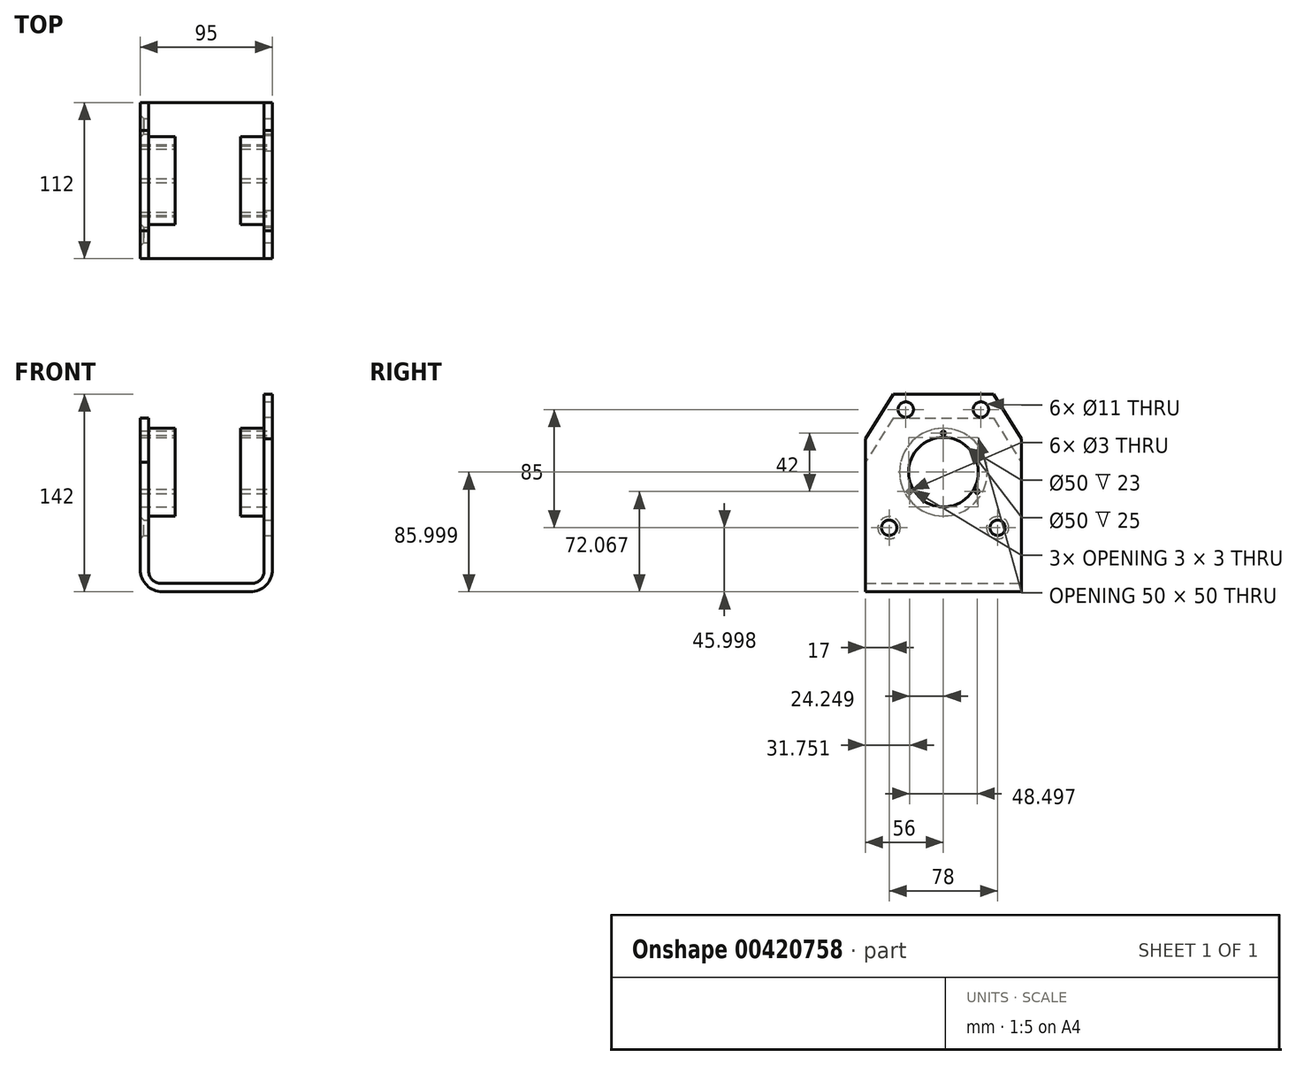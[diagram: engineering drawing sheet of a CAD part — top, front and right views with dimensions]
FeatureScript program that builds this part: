
annotation { "Feature Type Name" : "Feature", "Feature Type Description" : "" }
export const myFeature = defineFeature(function(context is Context, id is Id, definition is map)
    precondition{}
    {
        {
            var Q0;
            Q0=qCreatedBy(makeId("Front.planeOp"),FACE);
            var sketch = newSketch(context, id + "F0", { "sketchPlane" : qUnion([Q0])});
            skLineSegment(sketch, "E0.top", {"start": v(-43.8, -38.82) * mm, "end": v(19.2, -38.82) * mm});
            skLineSegment(sketch, "E0.right", {"start": v(35.2, 103.18) * mm, "end": v(35.2, -22.82) * mm});
            skLineSegment(sketch, "E1.top", {"start": v(-44.8, -32.82) * mm, "end": v(20.2, -32.82) * mm});
            skLineSegment(sketch, "E1.right", {"start": v(29.2, 103.18) * mm, "end": v(29.2, -23.82) * mm});
            skLineSegment(sketch, "E2", {"start": v(29.2, 103.18) * mm, "end": v(35.2, 103.18) * mm});
            skLineSegment(sketch, "E3.right", {"start": v(29.2, 103.18) * mm, "end": v(29.2, 87.18) * mm});
            skLineSegment(sketch, "E4", {"start": v(-53.8, -23.82) * mm, "end": v(-53.8, 86.18) * mm});
            skLineSegment(sketch, "E5", {"start": v(-53.8, 86.18) * mm, "end": v(-59.8, 86.18) * mm});
            skLineSegment(sketch, "E6", {"start": v(-59.8, 86.18) * mm, "end": v(-59.8, -22.82) * mm});
            skPoint(sketch, "E7.visualSharp", {"position": v(-53.8, -32.82) * mm});
            skArc(sketch, "E7.filletArc", {"start": v(-53.8, -23.82) * mm, "mid": v(-51.16, -30.19) * mm, "end": v(-44.8, -32.82) * mm});
            skPoint(sketch, "E8.visualSharp", {"position": v(-59.8, -38.82) * mm});
            skArc(sketch, "E8.filletArc", {"start": v(-59.8, -22.82) * mm, "mid": v(-55.1, -34.14) * mm, "end": v(-43.8, -38.82) * mm});
            skPoint(sketch, "E9.visualSharp", {"position": v(29.2, -32.82) * mm});
            skArc(sketch, "E9.filletArc", {"start": v(20.2, -32.82) * mm, "mid": v(26.57, -30.19) * mm, "end": v(29.2, -23.82) * mm});
            skPoint(sketch, "E10.visualSharp", {"position": v(35.2, -38.82) * mm});
            skArc(sketch, "E10.filletArc", {"start": v(19.2, -38.82) * mm, "mid": v(30.52, -34.14) * mm, "end": v(35.2, -22.82) * mm});
            skSolve(sketch);
        }
        {
            var Q0;
            Q0=makeQuery(id+"F0.imprint","IMPRINT",FACE,{"disambiguationData":[TD([[makeQuery(id+"F0.imprint","IMPRINT",EDGE,{"derivedFrom":sQuery(id+"F0.wireOp",EDGE,"E0.top")}),1.0]])]});
            extrude(context, id + "F1", {"entities" : qUnion([Q0]), "depth" : 112 * mm});
        }
        {
            var Q0;
            Q0=makeQuery(id+"F1.opExtrude","SWEPT_FACE",FACE,{"disambiguationData":[OSD([sQuery(id+"F0.wireOp",EDGE,"E0.right")])]});
            var sketch = newSketch(context, id + "F2", { "sketchPlane" : qUnion([Q0])});
            skCircle(sketch, "E11", {"center": v(-56, 47.18) * mm, "radius": 25 * mm});
            skCircle(sketch, "E12", {"center": v(-56, 47.18) * mm, "radius": 31.5 * mm});
            skSolve(sketch);
        }
        {
            var Q0;
            Q0=makeQuery(id+"F2.imprint","IMPRINT",FACE,{"disambiguationData":[TD([[makeQuery(id+"F2.imprint","IMPRINT",EDGE,{"derivedFrom":sQuery(id+"F2.wireOp",EDGE,"E11")}),1.0]])]});
            extrude(context, id + "F3", {"entities" : qUnion([Q0]), "operationType" : NewBodyOperationType.REMOVE, "oppositeDirection" : true, "depth" : 185 * mm});
        }
        {
            var Q0;
            Q0=makeQuery(id+"F1.opExtrude","CAP_FACE",FACE,{"disambiguationData":[OSD([sQuery(id+"F0.wireOp",EDGE,"E0.top"),sQuery(id+"F0.wireOp",EDGE,"E0.right"),sQuery(id+"F0.wireOp",EDGE,"E1.top"),sQuery(id+"F0.wireOp",EDGE,"E1.right"),sQuery(id+"F0.wireOp",EDGE,"E2"),sQuery(id+"F0.wireOp",EDGE,"E3.right"),sQuery(id+"F0.wireOp",EDGE,"E4"),sQuery(id+"F0.wireOp",EDGE,"E5"),sQuery(id+"F0.wireOp",EDGE,"E6"),sQuery(id+"F0.wireOp",EDGE,"E7.filletArc"),sQuery(id+"F0.wireOp",EDGE,"E8.filletArc"),sQuery(id+"F0.wireOp",EDGE,"E9.filletArc"),sQuery(id+"F0.wireOp",EDGE,"E10.filletArc")])],"isStart":false});
            cPlane(context, id + "F4", {"entities" : qUnion([Q0]), "cplaneType" : CPlaneType.OFFSET, "offset" : 25 * mm, "width" : 150 * mm, "height" : 150 * mm});
        }
        {
            var Q0;
            Q0=makeQuery(id+"F2.imprint","IMPRINT",FACE,{"disambiguationData":[TD([[makeQuery(id+"F2.imprint","IMPRINT",EDGE,{"derivedFrom":sQuery(id+"F2.wireOp",EDGE,"E11")}),-1.0]])]});
            extrude(context, id + "F5", {"entities" : qUnion([Q0]), "operationType" : NewBodyOperationType.REMOVE, "oppositeDirection" : true, "depth" : 184 * mm});
        }
        {
            var Q0;
            Q0=makeQuery(id+"F2.imprint","IMPRINT",FACE,{"disambiguationData":[TD([[makeQuery(id+"F2.imprint","IMPRINT",EDGE,{"derivedFrom":sQuery(id+"F2.wireOp",EDGE,"E11")}),-1.0]])]});
            extrude(context, id + "F6", {"entities" : qUnion([Q0]), "operationType" : NewBodyOperationType.ADD, "oppositeDirection" : true, "depth" : 95 * mm});
        }
        {
            var Q0;
            Q0=qCreatedBy(id+"F4.planeOp",FACE);
            var sketch = newSketch(context, id + "F7", { "sketchPlane" : qUnion([Q0])});
            skLineSegment(sketch, "E13.bottom", {"start": v(-34.8, 79.18) * mm, "end": v(12.2, 79.18) * mm});
            skLineSegment(sketch, "E13.top", {"start": v(-34.8, -20.82) * mm, "end": v(12.2, -20.82) * mm});
            skLineSegment(sketch, "E13.left", {"start": v(-34.8, 79.18) * mm, "end": v(-34.8, -20.82) * mm});
            skLineSegment(sketch, "E13.right", {"start": v(12.2, 79.18) * mm, "end": v(12.2, -20.82) * mm});
            skSolve(sketch);
        }
        {
            var Q0;
            Q0=makeQuery(id+"F7.imprint","IMPRINT",FACE,{"disambiguationData":[TD([[makeQuery(id+"F7.imprint","IMPRINT",EDGE,{"derivedFrom":sQuery(id+"F7.wireOp",EDGE,"E13.bottom")}),-1.0]])]});
            extrude(context, id + "F8", {"entities" : qUnion([Q0]), "operationType" : NewBodyOperationType.REMOVE, "oppositeDirection" : true, "depth" : 159 * mm});
        }
        {
            var Q0;
            Q0=makeQuery(id+"F2.imprint","IMPRINT",FACE,{"disambiguationData":[TD([[makeQuery(id+"F2.imprint","IMPRINT",EDGE,{"derivedFrom":sQuery(id+"F2.wireOp",EDGE,"E12")}),-1.0]])]});
            var sketch = newSketch(context, id + "F9", { "sketchPlane" : qUnion([Q0])});
            skCircle(sketch, "E14", {"center": v(-83, 92.18) * mm, "radius": 5.5 * mm});
            skCircle(sketch, "E15", {"center": v(-29, 92.18) * mm, "radius": 5.5 * mm});
            skCircle(sketch, "E16", {"center": v(-95, 7.18) * mm, "radius": 5.5 * mm});
            skCircle(sketch, "E17", {"center": v(-17, 7.18) * mm, "radius": 5.5 * mm});
            skPoint(sketch, "E18", {"position": v(-56, 47.25) * mm});
            skPoint(sketch, "E19", {"position": v(-80.25, 33.25) * mm});
            skPoint(sketch, "E20", {"position": v(-31.75, 33.25) * mm});
            skPoint(sketch, "E21", {"position": v(-56, 75.25) * mm});
            skCircle(sketch, "E22", {"center": v(-80.25, 33.25) * mm, "radius": 1.5 * mm});
            skCircle(sketch, "E23", {"center": v(-56, 75.25) * mm, "radius": 1.5 * mm});
            skCircle(sketch, "E24", {"center": v(-31.75, 33.25) * mm, "radius": 1.5 * mm});
            skLineSegment(sketch, "E25", {"start": v(-56, 75.25) * mm, "end": v(-56, 47.25) * mm});
            skSolve(sketch);
        }
        {
            var Q0;
            Q0=makeQuery(id+"F9.imprint","IMPRINT",FACE,{"disambiguationData":[TD([[makeQuery(id+"F9.imprint","IMPRINT",EDGE,{"derivedFrom":sQuery(id+"F9.wireOp",EDGE,"E14")}),1.0]])]});
            var Q1;
            Q1=makeQuery(id+"F9.imprint","IMPRINT",FACE,{"disambiguationData":[TD([[makeQuery(id+"F9.imprint","IMPRINT",EDGE,{"derivedFrom":sQuery(id+"F9.wireOp",EDGE,"E15")}),1.0]])]});
            var Q2;
            Q2=makeQuery(id+"F9.imprint","IMPRINT",FACE,{"disambiguationData":[TD([[makeQuery(id+"F9.imprint","IMPRINT",EDGE,{"derivedFrom":sQuery(id+"F9.wireOp",EDGE,"E16")}),1.0]])]});
            var Q3;
            Q3=makeQuery(id+"F9.imprint","IMPRINT",FACE,{"disambiguationData":[TD([[makeQuery(id+"F9.imprint","IMPRINT",EDGE,{"derivedFrom":sQuery(id+"F9.wireOp",EDGE,"E17")}),1.0]])]});
            extrude(context, id + "F10", {"entities" : qUnion([Q0, Q1, Q2, Q3]), "operationType" : NewBodyOperationType.REMOVE, "oppositeDirection" : true, "depth" : 157.2 * mm});
        }
        {
            var Q0;
            Q0=makeQuery(id+"F9.imprint","IMPRINT",FACE,{"disambiguationData":[TD([[makeQuery(id+"F9.imprint","IMPRINT",EDGE,{"derivedFrom":sQuery(id+"F9.wireOp",EDGE,"E24")}),1.0]])]});
            var Q1;
            Q1=makeQuery(id+"F9.imprint","IMPRINT",FACE,{"disambiguationData":[TD([[makeQuery(id+"F9.imprint","IMPRINT",EDGE,{"derivedFrom":sQuery(id+"F9.wireOp",EDGE,"E22")}),1.0]])]});
            var Q2;
            Q2=makeQuery(id+"F9.imprint","IMPRINT",FACE,{"disambiguationData":[TD([[makeQuery(id+"F9.imprint","IMPRINT",EDGE,{"derivedFrom":sQuery(id+"F9.wireOp",EDGE,"E23")}),1.0]])]});
            extrude(context, id + "F11", {"entities" : qUnion([Q0, Q1, Q2]), "operationType" : NewBodyOperationType.REMOVE, "oppositeDirection" : true, "depth" : 154.4 * mm});
        }
        {
            var Q0;
            Q0=makeQuery(id+"F1.opExtrude","CAP_EDGE",EDGE,{"disambiguationData":[OSD([sQuery(id+"F0.wireOp",EDGE,"E5")])],"isStart":true});
            var Q1;
            Q1=makeQuery(id+"F1.opExtrude","CAP_EDGE",EDGE,{"disambiguationData":[OSD([sQuery(id+"F0.wireOp",EDGE,"E2")])],"isStart":true});
            var Q2;
            Q2=makeQuery(id+"F1.opExtrude","CAP_EDGE",EDGE,{"disambiguationData":[OSD([sQuery(id+"F0.wireOp",EDGE,"E5")])],"isStart":false});
            var Q3;
            Q3=makeQuery(id+"F1.opExtrude","CAP_EDGE",EDGE,{"disambiguationData":[OSD([sQuery(id+"F0.wireOp",EDGE,"E2")])],"isStart":false});
            chamfer(context, id + "F12", {"entities" : qUnion([Q0, Q1, Q2, Q3]), "chamferType" : ChamferType.TWO_OFFSETS, "width1" : 20 * mm, "oppositeDirection" : false, "width2" : 32 * mm, "tangentPropagation" : true});
        }
        {
            var Q0;
            Q0=makeQuery(id+"F10.boolean.opBoolean","INTERSECT",EDGE,{"derivedFrom":[makeQuery(id+"F6.boolean.opBoolean","MERGE",FACE,{"derivedFrom":[makeQuery(id+"F1.opExtrude","SWEPT_FACE",FACE,{"disambiguationData":[OSD([sQuery(id+"F0.wireOp",EDGE,"E6")])]}),makeQuery(id+"F6.opExtrude","CAP_FACE",FACE,{"disambiguationData":[OSD([sQuery(id+"F2.wireOp",EDGE,"E11"),sQuery(id+"F2.wireOp",EDGE,"E12")])],"isStart":false})]}),makeQuery(id+"F10.opExtrude","SWEPT_FACE",FACE,{"disambiguationData":[OSD([sQuery(id+"F9.wireOp",EDGE,"E17")])]})]});
            var Q1;
            Q1=makeQuery(id+"F10.boolean.opBoolean","INTERSECT",EDGE,{"derivedFrom":[makeQuery(id+"F6.boolean.opBoolean","MERGE",FACE,{"derivedFrom":[makeQuery(id+"F1.opExtrude","SWEPT_FACE",FACE,{"disambiguationData":[OSD([sQuery(id+"F0.wireOp",EDGE,"E6")])]}),makeQuery(id+"F6.opExtrude","CAP_FACE",FACE,{"disambiguationData":[OSD([sQuery(id+"F2.wireOp",EDGE,"E11"),sQuery(id+"F2.wireOp",EDGE,"E12")])],"isStart":false})]}),makeQuery(id+"F10.opExtrude","SWEPT_FACE",FACE,{"disambiguationData":[OSD([sQuery(id+"F9.wireOp",EDGE,"E16")])]})]});
            chamfer(context, id + "F13", {"entities" : qUnion([Q0, Q1]), "width" : 2.5 * mm, "tangentPropagation" : true});
        }
    });
